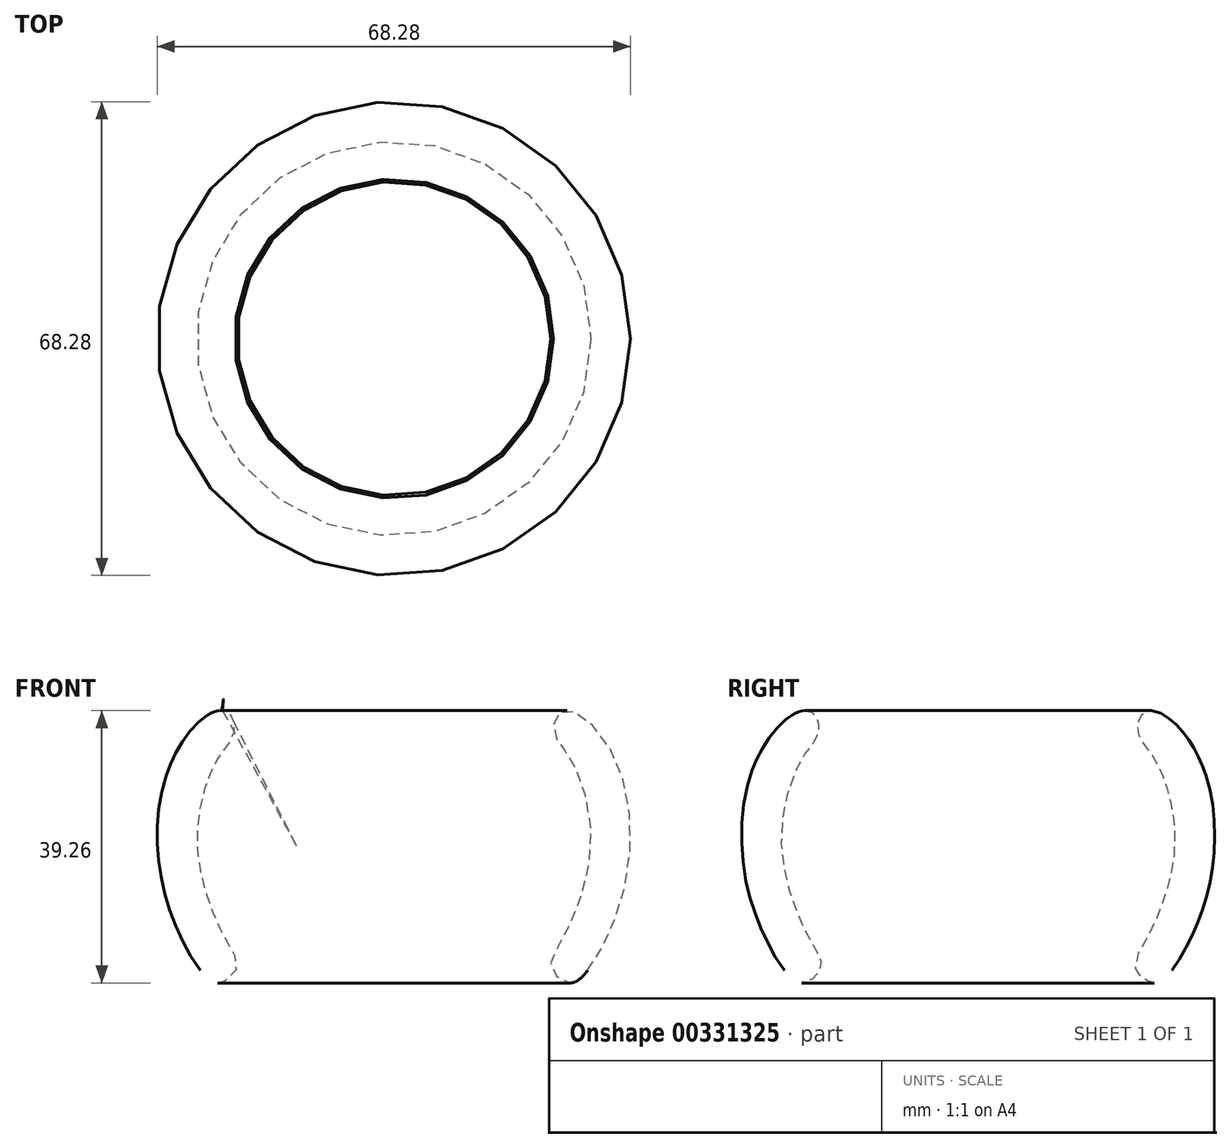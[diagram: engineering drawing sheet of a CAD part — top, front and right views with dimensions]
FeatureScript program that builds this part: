
annotation { "Feature Type Name" : "Feature", "Feature Type Description" : "" }
export const myFeature = defineFeature(function(context is Context, id is Id, definition is map)
    precondition{}
    {
        {
            var Q0;
            Q0=qCreatedBy(makeId("Front.planeOp"),FACE);
            var sketch = newSketch(context, id + "F0", { "sketchPlane" : qUnion([Q0])});
            skFitSpline(sketch, "E0", {"points": [v(27.93, -9.3) * mm, v(33.37, 3.08) * mm, v(31.99, 21.1) * mm, v(25.45, 28.13) * mm, v(23.27, 27.14) * mm, v(23.37, 24.27) * mm, v(25.35, 21.4) * mm, v(28.42, 9.12) * mm, v(24.17, -5.03) * mm, v(22.68, -8.9) * mm, v(25.16, -11.07) * mm, v(27.93, -9.3) * mm]});
            skSolve(sketch);
        }
        {
            var Q0;
            Q0=qCreatedBy(makeId("Front.planeOp"),FACE);
            var sketch = newSketch(context, id + "F1", { "sketchPlane" : qUnion([Q0])});
            skLineSegment(sketch, "E1", {"start": v(0, -36.55) * mm, "end": v(0, 51.55) * mm, "construction": true});
            skSolve(sketch);
        }
        {
            var Q0;
            Q0 = qSketchRegion(id + "F0", true);
            var Q1;
            Q1=sQuery(id+"F1.wireOp",EDGE,"E1");
            revolve(context, id + "F2", {"entities" : qUnion([Q0]), "axis" : qUnion([Q1]), "revolveType" : RevolveType.FULL});
        }
    });
